# Revit family: ASSA_ABLOY_CurvedCD
name_source: partatom
category: Doors
units: mm (PartAtom-declared; Revit-internal decimal feet)

## family parameters
Always vertical = Yes
Cut with Voids When Loaded = No
Host = Wall
Room Calculation Point = No
Shared = No

## types (1)
- Curved
    Analytic Construction = <None>
    Assembly Code = B2030300
    BreakoutFacility = No
    Colour = Customer specific
    Cost = 0 $
    Define Thermal Properties by = Schematic Type
    Description = Curved Sliding Door
    DrumWallOptions = Glass, Sandwich panel
    FireExit = No
    FrameSeal = Yes
    GlassLayers = 0
    GlassThickness1 = 0 mm  [stored 0 ft]
    GlassThickness2 = 0 mm  [stored 0 ft]
    HandicapAccessible = Yes
    HasDrive = Yes
    IsExternal = Yes
    ManufacturerURL = www.record.group
    Material = Aluminium
    Model = K31
    ModelReference = Depends on the configuration
    NominalHeight = 0 mm  [stored 0 ft]
    NominalLength = 0 mm  [stored 0 ft]
    NominalWidth = 0 mm  [stored 0 ft]
    ReplacementCost = Depends on the configuration and door type
    SelfClosing = Yes
    Shape = Rectangular shaped
    URL = www.agta-record.com
    WarrantyDescription = Depends on country
    Weight = Depends on configuration and size

note: [stored X ft] marks values corroborated as IEEE doubles in the binary element streams (Revit-internal decimal feet)

## geometry (parser evidence)
native form markers: Sweep x21
no freeform markers — native parametric forms only
